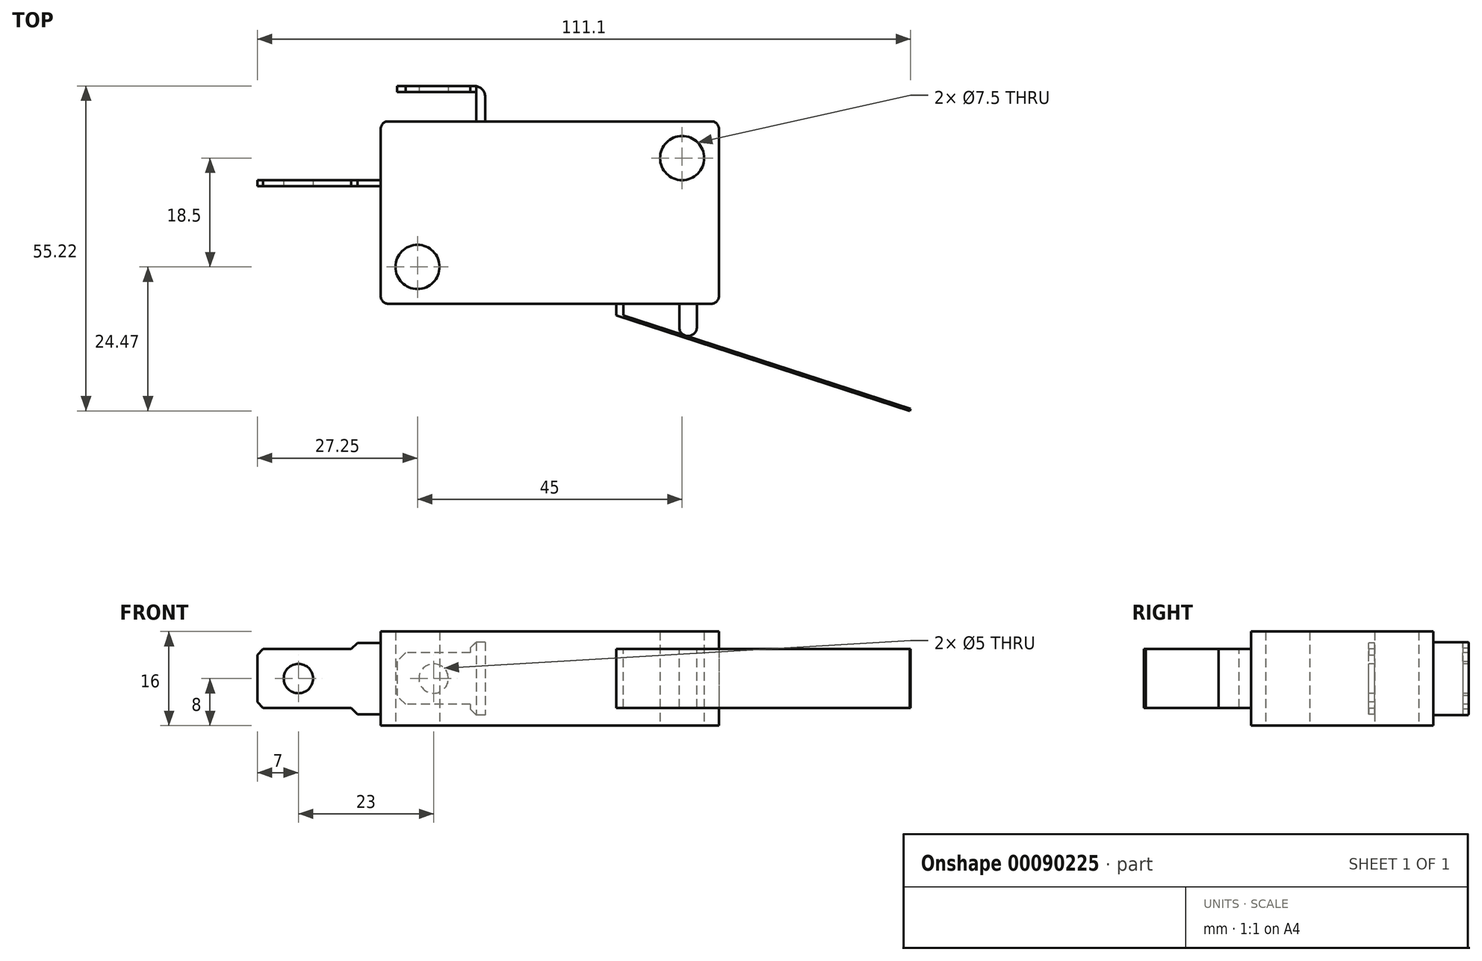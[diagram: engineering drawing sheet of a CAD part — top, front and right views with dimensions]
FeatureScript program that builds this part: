
annotation { "Feature Type Name" : "Feature", "Feature Type Description" : "" }
export const myFeature = defineFeature(function(context is Context, id is Id, definition is map)
    precondition{}
    {
        {
            var Q0;
            Q0=qCreatedBy(makeId("Top.planeOp"),FACE);
            var sketch = newSketch(context, id + "F0", { "sketchPlane" : qUnion([Q0])});
            skLineSegment(sketch, "E0.bottom", {"start": v(0, 0) * mm, "end": v(57.5, 0) * mm});
            skLineSegment(sketch, "E0.top", {"start": v(0, -31) * mm, "end": v(57.5, -31) * mm});
            skLineSegment(sketch, "E0.left", {"start": v(0, 0) * mm, "end": v(0, -31) * mm});
            skLineSegment(sketch, "E0.right", {"start": v(57.5, 0) * mm, "end": v(57.5, -31) * mm});
            skCircle(sketch, "E1", {"center": v(1.25, -1.25) * mm, "radius": 1.25 * mm});
            skCircle(sketch, "E2", {"center": v(1.25, -29.75) * mm, "radius": 1.25 * mm});
            skCircle(sketch, "E3", {"center": v(56.25, -29.75) * mm, "radius": 1.25 * mm});
            skCircle(sketch, "E4", {"center": v(56.25, -1.25) * mm, "radius": 1.25 * mm});
            skCircle(sketch, "E5", {"center": v(6.25, -24.75) * mm, "radius": 3.75 * mm});
            skCircle(sketch, "E6", {"center": v(51.25, -6.25) * mm, "radius": 3.75 * mm});
            skSolve(sketch);
        }
        {
            var Q0;
            {var subQ0=sQuery(id+"F0.wireOp",EDGE,"E1");var subQ1=makeQuery(id+"F0.imprint","INTERSECT",VERTEX,{"derivedFrom":[sQuery(id+"F0.wireOp",EDGE,"E0.bottom"),subQ0]});Q0=makeQuery(id+"F0.imprint","IMPRINT",FACE,{"disambiguationData":[TD([[makeQuery(id+"F0.imprint","IMPRINT",EDGE,{"disambiguationData":[TD([[subQ1,-1.0]])],"derivedFrom":subQ0}),1.0]])]});}
            var Q1;
            {var subQ0=sQuery(id+"F0.wireOp",EDGE,"E2");var subQ1=makeQuery(id+"F0.imprint","INTERSECT",VERTEX,{"derivedFrom":[sQuery(id+"F0.wireOp",EDGE,"E0.top"),subQ0]});Q1=makeQuery(id+"F0.imprint","IMPRINT",FACE,{"disambiguationData":[TD([[makeQuery(id+"F0.imprint","IMPRINT",EDGE,{"disambiguationData":[TD([[subQ1,1.0]])],"derivedFrom":subQ0}),1.0]])]});}
            var Q2;
            {var subQ0=sQuery(id+"F0.wireOp",EDGE,"E3");var subQ1=makeQuery(id+"F0.imprint","INTERSECT",VERTEX,{"derivedFrom":[sQuery(id+"F0.wireOp",EDGE,"E0.top"),subQ0]});Q2=makeQuery(id+"F0.imprint","IMPRINT",FACE,{"disambiguationData":[TD([[makeQuery(id+"F0.imprint","IMPRINT",EDGE,{"disambiguationData":[TD([[subQ1,1.0]])],"derivedFrom":subQ0}),1.0]])]});}
            var Q3;
            {var subQ0=sQuery(id+"F0.wireOp",EDGE,"E4");var subQ1=makeQuery(id+"F0.imprint","INTERSECT",VERTEX,{"derivedFrom":[sQuery(id+"F0.wireOp",EDGE,"E0.bottom"),subQ0]});Q3=makeQuery(id+"F0.imprint","IMPRINT",FACE,{"disambiguationData":[TD([[makeQuery(id+"F0.imprint","IMPRINT",EDGE,{"disambiguationData":[TD([[subQ1,1.0]])],"derivedFrom":subQ0}),1.0]])]});}
            var Q4;
            Q4=makeQuery(id+"F0.imprint","IMPRINT",FACE,{"disambiguationData":[TD([[makeQuery(id+"F0.imprint","IMPRINT",EDGE,{"derivedFrom":sQuery(id+"F0.wireOp",EDGE,"E5")}),-1.0]])]});
            extrude(context, id + "F1", {"entities" : qUnion([Q0, Q1, Q2, Q3, Q4]), "depth" : 16 * mm});
        }
        {
            var Q0;
            Q0=makeQuery(id+"F1.opExtrude","SWEPT_FACE",FACE,{"disambiguationData":[OSD([sQuery(id+"F0.wireOp",EDGE,"E0.top")])]});
            var sketch = newSketch(context, id + "F2", { "sketchPlane" : qUnion([Q0])});
            skLineSegment(sketch, "E7.bottom", {"start": v(0, 3) * mm, "end": v(-21, 3) * mm});
            skLineSegment(sketch, "E7.top", {"start": v(0, 13) * mm, "end": v(-21, 13) * mm});
            skLineSegment(sketch, "E7.left", {"start": v(0, 3) * mm, "end": v(0, 13) * mm});
            skLineSegment(sketch, "E7.right", {"start": v(-21, 3) * mm, "end": v(-21, 13) * mm});
            skLineSegment(sketch, "E8", {"start": v(-5, 13) * mm, "end": v(-3.94, 14.06) * mm});
            skLineSegment(sketch, "E9", {"start": v(-3.94, 14.06) * mm, "end": v(0, 14.06) * mm});
            skLineSegment(sketch, "E10", {"start": v(-5, 3) * mm, "end": v(-3.94, 1.94) * mm});
            skLineSegment(sketch, "E11", {"start": v(-3.94, 1.94) * mm, "end": v(0, 1.94) * mm});
            skCircle(sketch, "E12", {"center": v(-14, 8) * mm, "radius": 2.5 * mm});
            skLineSegment(sketch, "E13", {"start": v(0, 13) * mm, "end": v(0, 14.06) * mm});
            skLineSegment(sketch, "E14", {"start": v(0, 1.94) * mm, "end": v(0, 3) * mm});
            skSolve(sketch);
        }
        {
            var Q0;
            Q0 = qSketchRegion(id + "F2", true);
            extrude(context, id + "F3", {"entities" : qUnion([Q0]), "operationType" : NewBodyOperationType.ADD, "oppositeDirection" : true, "depth" : 21 * mm, "hasSecondDirection" : true, "secondDirectionOppositeDirection" : true, "secondDirectionDepth" : 20 * mm});
        }
        {
            var Q0;
            Q0=makeQuery(id+"F3.opExtrude","SWEPT_EDGE",EDGE,{"disambiguationData":[OSD([sQuery(id+"F2.wireOp",EDGE,"E7.top"),sQuery(id+"F2.wireOp",EDGE,"E7.right")])]});
            chamfer(context, id + "F4", {"entities" : qUnion([Q0]), "width" : 1 * mm, "tangentPropagation" : true});
        }
        {
            var Q0;
            Q0=makeQuery(id+"F3.opExtrude","SWEPT_EDGE",EDGE,{"disambiguationData":[OSD([sQuery(id+"F2.wireOp",EDGE,"E7.bottom"),sQuery(id+"F2.wireOp",EDGE,"E7.right")])]});
            chamfer(context, id + "F5", {"entities" : qUnion([Q0]), "width" : 1 * mm, "tangentPropagation" : true});
        }
        {
            var Q0;
            Q0=makeQuery(id+"F1.opExtrude","SWEPT_FACE",FACE,{"disambiguationData":[OSD([sQuery(id+"F0.wireOp",EDGE,"E0.bottom")])]});
            var sketch = newSketch(context, id + "F6", { "sketchPlane" : qUnion([Q0])});
            skLineSegment(sketch, "E15.bottom", {"start": v(-17.75, 14.2) * mm, "end": v(-16.25, 14.2) * mm});
            skLineSegment(sketch, "E15.top", {"start": v(-17.75, 1.8) * mm, "end": v(-16.25, 1.8) * mm});
            skLineSegment(sketch, "E15.left", {"start": v(-17.75, 14.2) * mm, "end": v(-17.75, 1.8) * mm});
            skLineSegment(sketch, "E15.right", {"start": v(-16.25, 14.2) * mm, "end": v(-16.25, 1.8) * mm});
            skSolve(sketch);
        }
        {
            var Q0;
            Q0 = qSketchRegion(id + "F6", true);
            extrude(context, id + "F7", {"entities" : qUnion([Q0]), "operationType" : NewBodyOperationType.ADD, "depth" : 5 * mm});
        }
        {
            var Q0;
            Q0=makeQuery(id+"F7.opExtrude","CAP_FACE",FACE,{"disambiguationData":[OSD([sQuery(id+"F6.wireOp",EDGE,"E15.bottom"),sQuery(id+"F6.wireOp",EDGE,"E15.top"),sQuery(id+"F6.wireOp",EDGE,"E15.left"),sQuery(id+"F6.wireOp",EDGE,"E15.right")])],"isStart":false});
            var sketch = newSketch(context, id + "F8", { "sketchPlane" : qUnion([Q0])});
            skLineSegment(sketch, "E16.bottom", {"start": v(-17.75, 14.2) * mm, "end": v(-15.25, 14.2) * mm});
            skLineSegment(sketch, "E16.top", {"start": v(-17.75, 1.8) * mm, "end": v(-15.25, 1.8) * mm});
            skLineSegment(sketch, "E16.left", {"start": v(-17.75, 14.2) * mm, "end": v(-17.75, 1.8) * mm});
            skLineSegment(sketch, "E16.right", {"start": v(-15.25, 14.2) * mm, "end": v(-15.25, 1.8) * mm});
            skLineSegment(sketch, "E17.bottom", {"start": v(-15.25, 12.4) * mm, "end": v(-2.75, 12.4) * mm});
            skLineSegment(sketch, "E17.top", {"start": v(-15.25, 3.6) * mm, "end": v(-2.75, 3.6) * mm});
            skLineSegment(sketch, "E17.left", {"start": v(-15.25, 12.4) * mm, "end": v(-15.25, 3.6) * mm});
            skLineSegment(sketch, "E17.right", {"start": v(-2.75, 12.4) * mm, "end": v(-2.75, 3.6) * mm});
            skCircle(sketch, "E18", {"center": v(-9, 8) * mm, "radius": 2.5 * mm});
            skLineSegment(sketch, "E19", {"start": v(-9, 12.4) * mm, "end": v(-9, 3.6) * mm, "construction": true});
            skSolve(sketch);
        }
        {
            var Q0;
            Q0 = qSketchRegion(id + "F8", true);
            extrude(context, id + "F9", {"entities" : qUnion([Q0]), "operationType" : NewBodyOperationType.ADD, "depth" : 1 * mm});
        }
        {
            var Q0;
            Q0=makeQuery(id+"F9.opExtrude","CAP_EDGE",EDGE,{"disambiguationData":[OSD([sQuery(id+"F8.wireOp",EDGE,"E16.left")])],"isStart":false});
            fillet(context, id + "F10", {"entities" : qUnion([Q0]), "radius" : 1.8 * mm, "tangentPropagation" : true, "allowEdgeOverflow" : false});
        }
        {
            var Q0;
            Q0=makeQuery(id+"F9.opExtrude","SWEPT_EDGE",EDGE,{"disambiguationData":[OSD([sQuery(id+"F8.wireOp",EDGE,"E16.top"),sQuery(id+"F8.wireOp",EDGE,"E16.right")])]});
            var Q1;
            Q1=makeQuery(id+"F9.opExtrude","SWEPT_EDGE",EDGE,{"disambiguationData":[OSD([sQuery(id+"F8.wireOp",EDGE,"E16.bottom"),sQuery(id+"F8.wireOp",EDGE,"E16.right")])]});
            chamfer(context, id + "F11", {"entities" : qUnion([Q0, Q1]), "width" : 1 * mm, "tangentPropagation" : true});
        }
        {
            var Q0;
            Q0=makeQuery(id+"F9.opExtrude","SWEPT_EDGE",EDGE,{"disambiguationData":[OSD([sQuery(id+"F8.wireOp",EDGE,"E17.top"),sQuery(id+"F8.wireOp",EDGE,"E17.right")])]});
            var Q1;
            Q1=makeQuery(id+"F9.opExtrude","SWEPT_EDGE",EDGE,{"disambiguationData":[OSD([sQuery(id+"F8.wireOp",EDGE,"E17.bottom"),sQuery(id+"F8.wireOp",EDGE,"E17.right")])]});
            chamfer(context, id + "F12", {"entities" : qUnion([Q0, Q1]), "width" : 1.5 * mm, "tangentPropagation" : true});
        }
        {
            var Q0;
            Q0=makeQuery(id+"F1.opExtrude","CAP_FACE",FACE,{"disambiguationData":[OSD([sQuery(id+"F0.wireOp",EDGE,"E0.bottom"),sQuery(id+"F0.wireOp",EDGE,"E0.top"),sQuery(id+"F0.wireOp",EDGE,"E0.left"),sQuery(id+"F0.wireOp",EDGE,"E0.right"),sQuery(id+"F0.wireOp",EDGE,"E1"),sQuery(id+"F0.wireOp",EDGE,"E2"),sQuery(id+"F0.wireOp",EDGE,"E3"),sQuery(id+"F0.wireOp",EDGE,"E4"),sQuery(id+"F0.wireOp",EDGE,"E5"),sQuery(id+"F0.wireOp",EDGE,"E6")])],"isStart":false});
            var sketch = newSketch(context, id + "F13", { "sketchPlane" : qUnion([Q0])});
            skLineSegment(sketch, "E20.bottom", {"start": v(40.05, -31) * mm, "end": v(41.25, -31) * mm});
            skLineSegment(sketch, "E20.top", {"start": v(40.05, -33) * mm, "end": v(41.25, -33) * mm});
            skLineSegment(sketch, "E20.left", {"start": v(40.05, -31) * mm, "end": v(40.05, -33) * mm});
            skLineSegment(sketch, "E20.right", {"start": v(41.25, -31) * mm, "end": v(41.25, -33) * mm});
            skLineSegment(sketch, "E21", {"start": v(40.05, -33) * mm, "end": v(89.98, -49.22) * mm});
            skLineSegment(sketch, "E22", {"start": v(41.25, -33) * mm, "end": v(90.1, -48.87) * mm});
            skLineSegment(sketch, "E23", {"start": v(90.1, -48.87) * mm, "end": v(89.98, -49.22) * mm});
            skLineSegment(sketch, "E24.bottom", {"start": v(53.76, -31) * mm, "end": v(50.76, -31) * mm});
            skLineSegment(sketch, "E24.top", {"start": v(53.76, -35) * mm, "end": v(50.76, -35) * mm});
            skLineSegment(sketch, "E24.left", {"start": v(53.76, -31) * mm, "end": v(53.76, -35) * mm});
            skLineSegment(sketch, "E24.right", {"start": v(50.76, -31) * mm, "end": v(50.76, -35) * mm});
            skCircle(sketch, "E25", {"center": v(52.26, -35) * mm, "radius": 1.5 * mm});
            skSolve(sketch);
        }
        {
            var Q0;
            Q0 = qSketchRegion(id + "F13", true);
            extrude(context, id + "F14", {"entities" : qUnion([Q0]), "oppositeDirection" : true, "depth" : 13 * mm, "hasSecondDirection" : true, "secondDirectionOppositeDirection" : true, "secondDirectionDepth" : 3 * mm});
        }
    });
